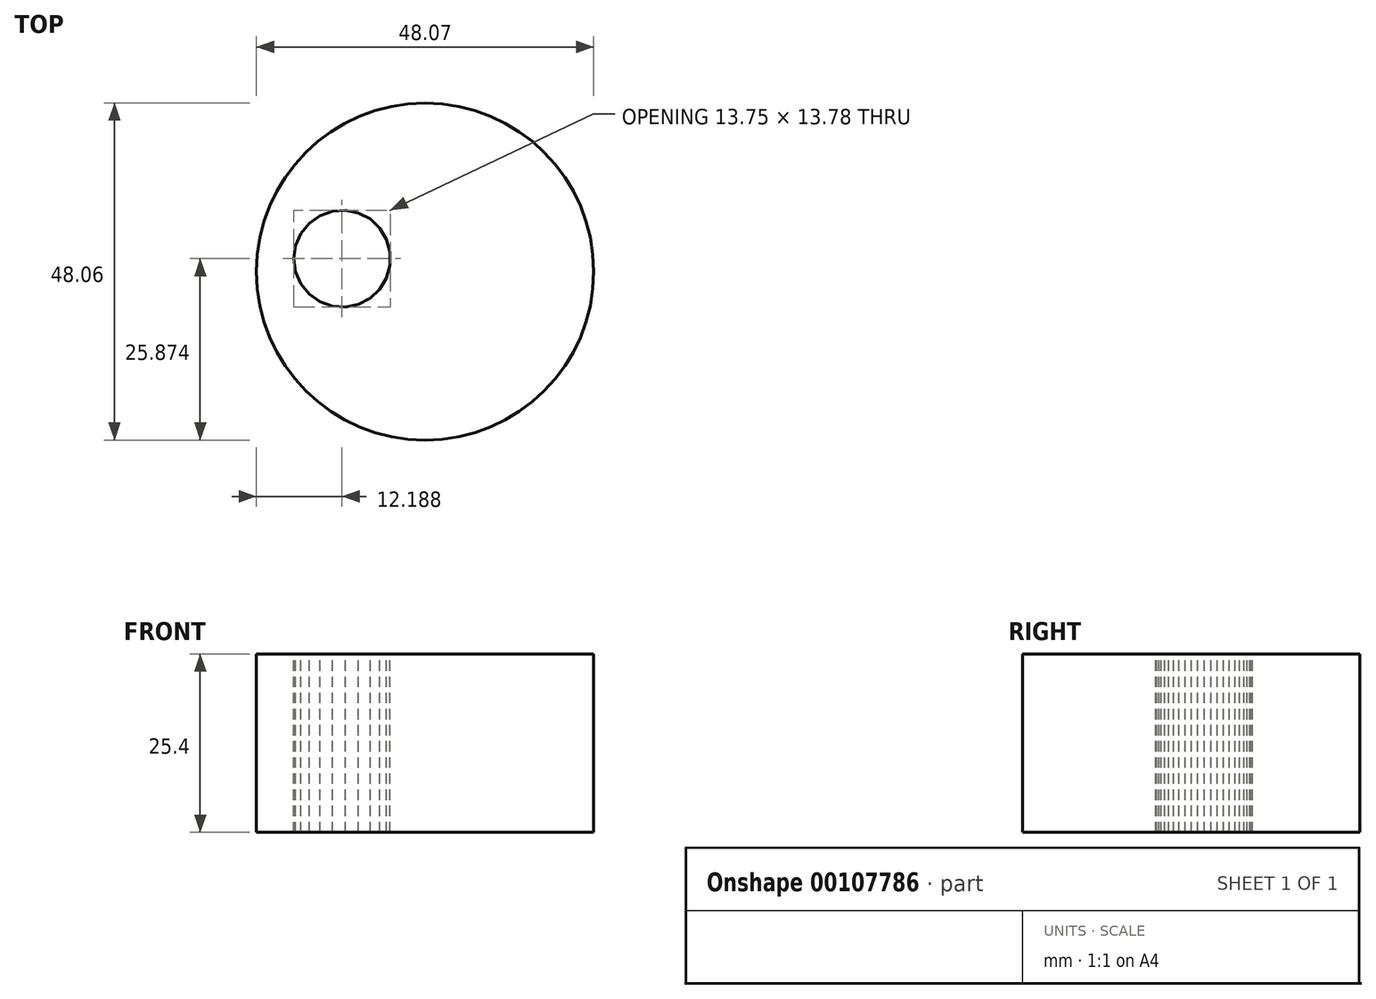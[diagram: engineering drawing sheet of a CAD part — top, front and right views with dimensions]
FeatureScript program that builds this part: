
annotation { "Feature Type Name" : "Feature", "Feature Type Description" : "" }
export const myFeature = defineFeature(function(context is Context, id is Id, definition is map)
    precondition{}
    {
        {
            var Q0;
            Q0=qCreatedBy(makeId("Top.planeOp"),FACE);
            var sketch = newSketch(context, id + "F0", { "sketchPlane" : qUnion([Q0])});
            skCircle(sketch, "E0", {"center": v(-54.66, -52.7) * mm, "radius": 24.03 * mm});
            skSolve(sketch);
        }
        {
            var Q0;
            Q0 = qSketchRegion(id + "F0", true);
            extrude(context, id + "F1", {"entities" : qUnion([Q0]), "depth" : 25.4 * mm});
        }
        {
            var Q0;
            Q0=makeQuery(id+"F1.opExtrude","CAP_FACE",FACE,{"disambiguationData":[OSD([sQuery(id+"F0.wireOp",EDGE,"E0")])],"isStart":false});
            var sketch = newSketch(context, id + "F2", { "sketchPlane" : qUnion([Q0])});
            skSolve(sketch);
        }
        {
            var Q0;
            Q0=makeQuery(id+"F2.imprint","IMPRINT",FACE,{"disambiguationData":[TD([[makeQuery(id+"F2.imprint","IMPRINT",EDGE,{"derivedFrom":makeQuery(id+"F1.opExtrude","CAP_EDGE",EDGE,{"disambiguationData":[OSD([sQuery(id+"F0.wireOp",EDGE,"E0")])],"isStart":false})}),1.0]])]});
            var sketch = newSketch(context, id + "F3", { "sketchPlane" : qUnion([Q0])});
            skCircle(sketch, "E1.cCircle", {"center": v(-66.47, -50.85) * mm, "radius": 6.84 * mm, "construction": true});
            skLineSegment(sketch, "E1.0", {"start": v(-59.63, -49.9) * mm, "end": v(-59.63, -51.79) * mm});
            skLineSegment(sketch, "E1.1", {"start": v(-59.63, -51.79) * mm, "end": v(-60.14, -53.6) * mm});
            skLineSegment(sketch, "E1.2", {"start": v(-60.14, -53.6) * mm, "end": v(-61.11, -55.2) * mm});
            skLineSegment(sketch, "E1.3", {"start": v(-61.11, -55.2) * mm, "end": v(-62.49, -56.49) * mm});
            skLineSegment(sketch, "E1.4", {"start": v(-62.49, -56.49) * mm, "end": v(-64.16, -57.35) * mm});
            skLineSegment(sketch, "E1.5", {"start": v(-64.16, -57.35) * mm, "end": v(-66, -57.74) * mm});
            skLineSegment(sketch, "E1.6", {"start": v(-66, -57.74) * mm, "end": v(-67.87, -57.6) * mm});
            skLineSegment(sketch, "E1.7", {"start": v(-67.87, -57.6) * mm, "end": v(-69.65, -56.98) * mm});
            skLineSegment(sketch, "E1.8", {"start": v(-69.65, -56.98) * mm, "end": v(-71.18, -55.9) * mm});
            skLineSegment(sketch, "E1.9", {"start": v(-71.18, -55.9) * mm, "end": v(-72.37, -54.43) * mm});
            skLineSegment(sketch, "E1.10", {"start": v(-72.37, -54.43) * mm, "end": v(-73.12, -52.7) * mm});
            skLineSegment(sketch, "E1.11", {"start": v(-73.12, -52.7) * mm, "end": v(-73.38, -50.85) * mm});
            skLineSegment(sketch, "E1.12", {"start": v(-73.38, -50.85) * mm, "end": v(-73.12, -48.98) * mm});
            skLineSegment(sketch, "E1.13", {"start": v(-73.12, -48.98) * mm, "end": v(-72.37, -47.26) * mm});
            skLineSegment(sketch, "E1.14", {"start": v(-72.37, -47.26) * mm, "end": v(-71.18, -45.8) * mm});
            skLineSegment(sketch, "E1.15", {"start": v(-71.18, -45.8) * mm, "end": v(-69.65, -44.71) * mm});
            skLineSegment(sketch, "E1.16", {"start": v(-69.65, -44.71) * mm, "end": v(-67.87, -44.08) * mm});
            skLineSegment(sketch, "E1.17", {"start": v(-67.87, -44.08) * mm, "end": v(-66, -43.96) * mm});
            skLineSegment(sketch, "E1.18", {"start": v(-66, -43.96) * mm, "end": v(-64.16, -44.34) * mm});
            skLineSegment(sketch, "E1.19", {"start": v(-64.16, -44.34) * mm, "end": v(-62.49, -45.2) * mm});
            skLineSegment(sketch, "E1.20", {"start": v(-62.49, -45.2) * mm, "end": v(-61.11, -46.49) * mm});
            skLineSegment(sketch, "E1.21", {"start": v(-61.11, -46.49) * mm, "end": v(-60.14, -48.1) * mm});
            skLineSegment(sketch, "E1.22", {"start": v(-60.14, -48.1) * mm, "end": v(-59.63, -49.9) * mm});
            skPoint(sketch, "E1.0.midPoint", {"position": v(-59.63, -50.85) * mm});
            skSolve(sketch);
        }
        {
            var Q0;
            Q0 = qSketchRegion(id + "F3", true);
            extrude(context, id + "F4", {"entities" : qUnion([Q0]), "operationType" : NewBodyOperationType.REMOVE, "oppositeDirection" : true, "depth" : 25.4 * mm});
        }
    });
